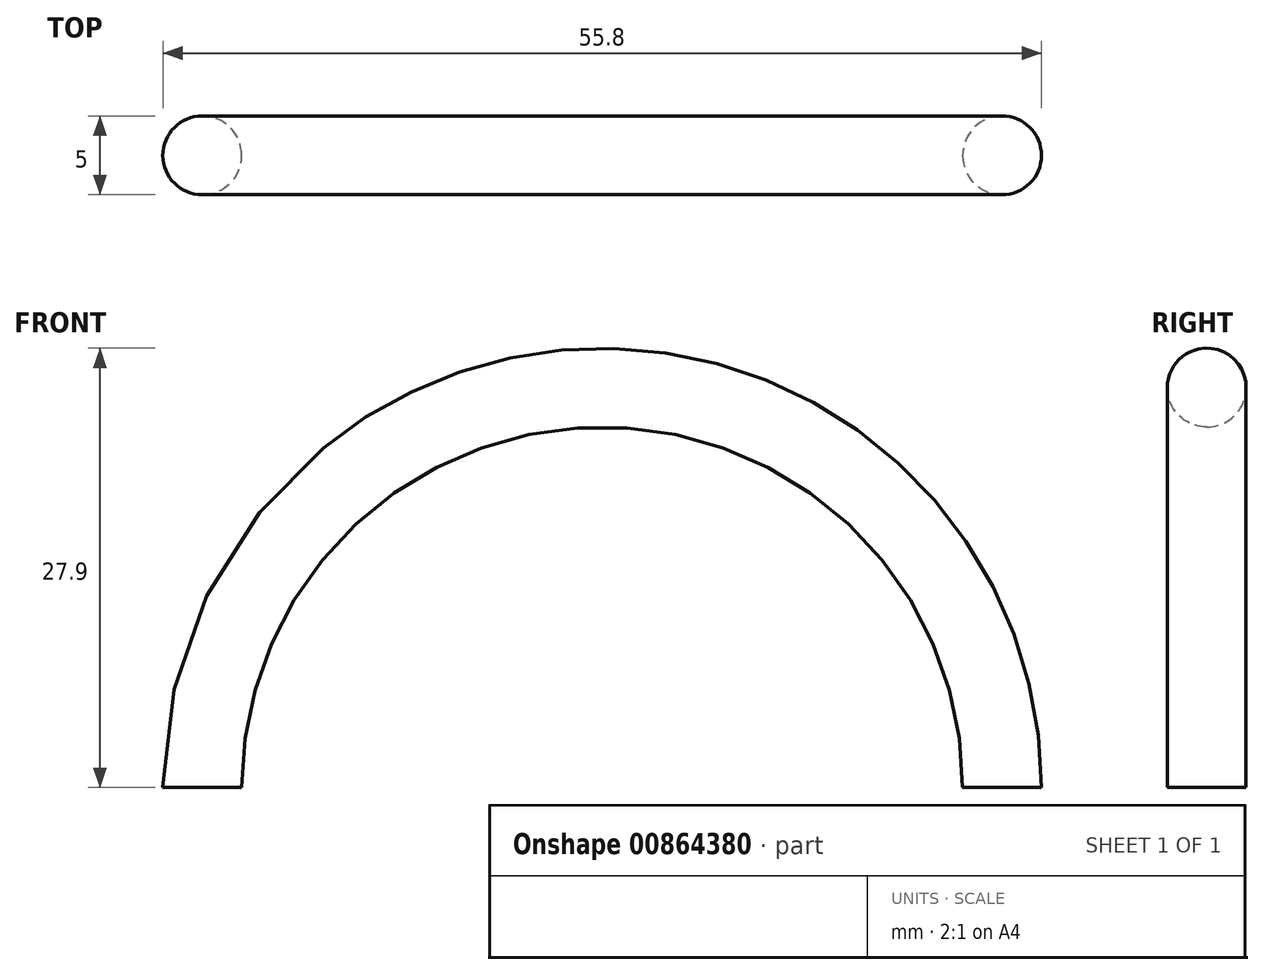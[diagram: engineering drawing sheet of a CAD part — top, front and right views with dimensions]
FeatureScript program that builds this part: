
annotation { "Feature Type Name" : "Feature", "Feature Type Description" : "" }
export const myFeature = defineFeature(function(context is Context, id is Id, definition is map)
    precondition{}
    {
        {
            var Q0;
            Q0=qCreatedBy(makeId("Front.planeOp"),FACE);
            var sketch = newSketch(context, id + "F0", { "sketchPlane" : qUnion([Q0])});
            skArc(sketch, "E0", {"start": v(50.8, 0) * mm, "mid": v(25.4, 25.4) * mm, "end": v(0, 0) * mm});
            skSolve(sketch);
        }
        {
            var Q0;
            Q0=qCreatedBy(makeId("Top.planeOp"),FACE);
            var sketch = newSketch(context, id + "F1", { "sketchPlane" : qUnion([Q0])});
            skCircle(sketch, "E1", {"center": v(0, 0) * mm, "radius": 2.5 * mm});
            skSolve(sketch);
        }
        {
            var Q0;
            Q0=makeQuery(id+"F1.imprint","IMPRINT",FACE,{"disambiguationData":[TD([[makeQuery(id+"F1.imprint","IMPRINT",EDGE,{"derivedFrom":sQuery(id+"F1.wireOp",EDGE,"E1")}),1.0]])]});
            var Q1;
            Q1 = qConstructionFilter(qBodyType(qCreatedBy(id + "F0" ,EDGE), BodyType.WIRE), ConstructionObject.NO);
            sweep(context, id + "F2", {"profiles" : qUnion([Q0]), "path" : qUnion([Q1])});
        }
    });
